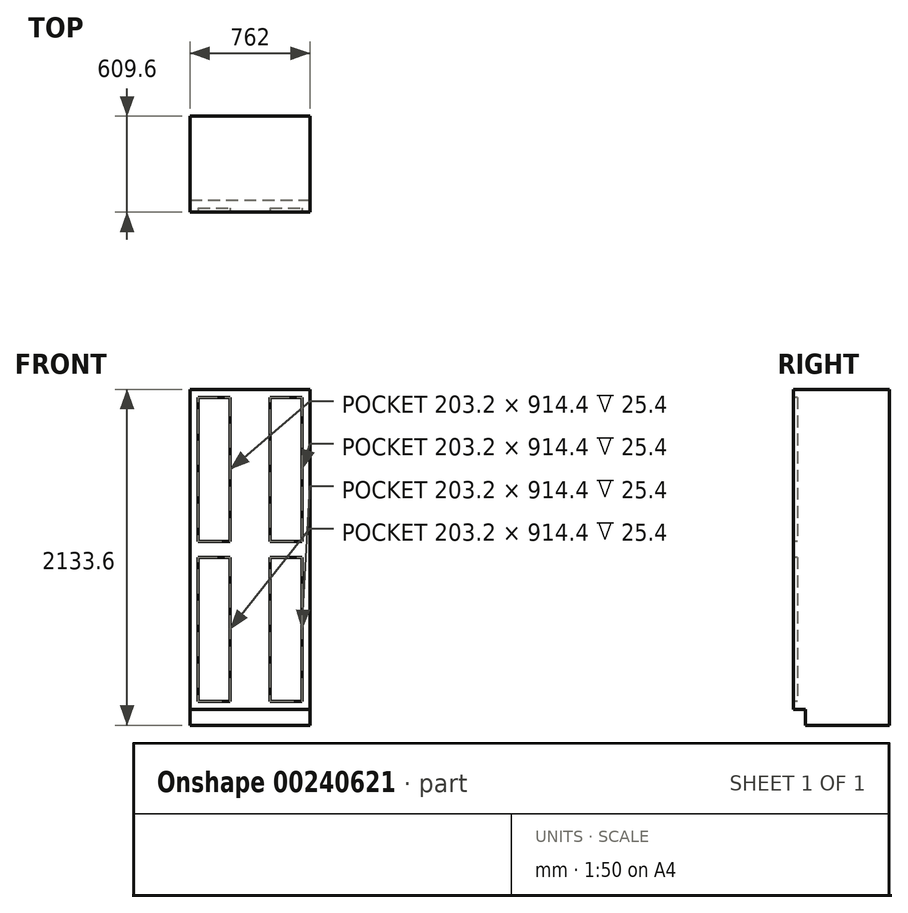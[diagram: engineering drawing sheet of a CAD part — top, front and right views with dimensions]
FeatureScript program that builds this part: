
annotation { "Feature Type Name" : "Feature", "Feature Type Description" : "" }
export const myFeature = defineFeature(function(context is Context, id is Id, definition is map)
    precondition{}
    {
        {
            var Q0;
            Q0=qCreatedBy(makeId("Top.planeOp"),FACE);
            var sketch = newSketch(context, id + "F0", { "sketchPlane" : qUnion([Q0])});
            skLineSegment(sketch, "E0.bottom", {"start": v(-304.8, 304.8) * mm, "end": v(457.2, 304.8) * mm});
            skLineSegment(sketch, "E0.top", {"start": v(-304.8, -304.8) * mm, "end": v(457.2, -304.8) * mm});
            skLineSegment(sketch, "E0.left", {"start": v(-304.8, 304.8) * mm, "end": v(-304.8, -304.8) * mm});
            skLineSegment(sketch, "E0.right", {"start": v(457.2, 304.8) * mm, "end": v(457.2, -304.8) * mm});
            skSolve(sketch);
        }
        {
            var Q0;
            Q0=makeQuery(id+"F0.imprint","IMPRINT",FACE,{"disambiguationData":[TD([[makeQuery(id+"F0.imprint","IMPRINT",EDGE,{"derivedFrom":sQuery(id+"F0.wireOp",EDGE,"E0.bottom")}),-1.0]])]});
            extrude(context, id + "F1", {"entities" : qUnion([Q0]), "depth" : 2133.6 * mm, "offsetDistance" : 25.4 * mm});
        }
        {
            var Q0;
            Q0=makeQuery(id+"F1.opExtrude","SWEPT_FACE",FACE,{"disambiguationData":[OSD([sQuery(id+"F0.wireOp",EDGE,"E0.top")])]});
            var sketch = newSketch(context, id + "F2", { "sketchPlane" : qUnion([Q0])});
            skLineSegment(sketch, "E1.bottom", {"start": v(-304.8, 0) * mm, "end": v(457.2, 0) * mm});
            skLineSegment(sketch, "E1.top", {"start": v(-304.8, 101.6) * mm, "end": v(457.2, 101.6) * mm});
            skLineSegment(sketch, "E1.left", {"start": v(-304.8, 0) * mm, "end": v(-304.8, 101.6) * mm});
            skLineSegment(sketch, "E1.right", {"start": v(457.2, 0) * mm, "end": v(457.2, 101.6) * mm});
            skSolve(sketch);
        }
        {
            var Q0;
            Q0=makeQuery(id+"F2.imprint","IMPRINT",FACE,{"disambiguationData":[TD([[makeQuery(id+"F2.imprint","IMPRINT",EDGE,{"derivedFrom":sQuery(id+"F2.wireOp",EDGE,"E1.bottom")}),1.0]])]});
            extrude(context, id + "F3", {"entities" : qUnion([Q0]), "operationType" : NewBodyOperationType.REMOVE, "oppositeDirection" : true, "depth" : 76.2 * mm, "offsetDistance" : 25.4 * mm});
        }
        {
            var Q0;
            Q0=makeQuery(id+"F1.opExtrude","SWEPT_FACE",FACE,{"disambiguationData":[OSD([sQuery(id+"F0.wireOp",EDGE,"E0.top")])]});
            var sketch = newSketch(context, id + "F4", { "sketchPlane" : qUnion([Q0])});
            skLineSegment(sketch, "E2.bottom", {"start": v(-254, 2082.8) * mm, "end": v(-50.8, 2082.8) * mm});
            skLineSegment(sketch, "E2.top", {"start": v(-254, 1168.4) * mm, "end": v(-50.8, 1168.4) * mm});
            skLineSegment(sketch, "E2.left", {"start": v(-254, 2082.8) * mm, "end": v(-254, 1168.4) * mm});
            skLineSegment(sketch, "E2.right", {"start": v(-50.8, 2082.8) * mm, "end": v(-50.8, 1168.4) * mm});
            skLineSegment(sketch, "E3.bottom", {"start": v(-254, 1066.8) * mm, "end": v(-50.8, 1066.8) * mm});
            skLineSegment(sketch, "E3.top", {"start": v(-254, 152.4) * mm, "end": v(-50.8, 152.4) * mm});
            skLineSegment(sketch, "E3.left", {"start": v(-254, 1066.8) * mm, "end": v(-254, 152.4) * mm});
            skLineSegment(sketch, "E3.right", {"start": v(-50.8, 1066.8) * mm, "end": v(-50.8, 152.4) * mm});
            skLineSegment(sketch, "E4.bottom", {"start": v(203.2, 2082.8) * mm, "end": v(406.4, 2082.8) * mm});
            skLineSegment(sketch, "E4.top", {"start": v(203.2, 1168.4) * mm, "end": v(406.4, 1168.4) * mm});
            skLineSegment(sketch, "E4.left", {"start": v(203.2, 2082.8) * mm, "end": v(203.2, 1168.4) * mm});
            skLineSegment(sketch, "E4.right", {"start": v(406.4, 2082.8) * mm, "end": v(406.4, 1168.4) * mm});
            skLineSegment(sketch, "E5.bottom", {"start": v(203.2, 1066.8) * mm, "end": v(406.4, 1066.8) * mm});
            skLineSegment(sketch, "E5.top", {"start": v(203.2, 152.4) * mm, "end": v(406.4, 152.4) * mm});
            skLineSegment(sketch, "E5.left", {"start": v(203.2, 1066.8) * mm, "end": v(203.2, 152.4) * mm});
            skLineSegment(sketch, "E5.right", {"start": v(406.4, 1066.8) * mm, "end": v(406.4, 152.4) * mm});
            skSolve(sketch);
        }
        {
            var Q0;
            Q0=makeQuery(id+"F4.imprint","IMPRINT",FACE,{"disambiguationData":[TD([[makeQuery(id+"F4.imprint","IMPRINT",EDGE,{"derivedFrom":sQuery(id+"F4.wireOp",EDGE,"E2.bottom")}),-1.0]])]});
            var Q1;
            Q1=makeQuery(id+"F4.imprint","IMPRINT",FACE,{"disambiguationData":[TD([[makeQuery(id+"F4.imprint","IMPRINT",EDGE,{"derivedFrom":sQuery(id+"F4.wireOp",EDGE,"E4.bottom")}),-1.0]])]});
            var Q2;
            Q2=makeQuery(id+"F4.imprint","IMPRINT",FACE,{"disambiguationData":[TD([[makeQuery(id+"F4.imprint","IMPRINT",EDGE,{"derivedFrom":sQuery(id+"F4.wireOp",EDGE,"E5.bottom")}),-1.0]])]});
            var Q3;
            Q3=makeQuery(id+"F4.imprint","IMPRINT",FACE,{"disambiguationData":[TD([[makeQuery(id+"F4.imprint","IMPRINT",EDGE,{"derivedFrom":sQuery(id+"F4.wireOp",EDGE,"E3.bottom")}),-1.0]])]});
            extrude(context, id + "F5", {"entities" : qUnion([Q0, Q1, Q2, Q3]), "operationType" : NewBodyOperationType.REMOVE, "oppositeDirection" : true, "depth" : 25.4 * mm, "offsetDistance" : 25.4 * mm});
        }
    });
